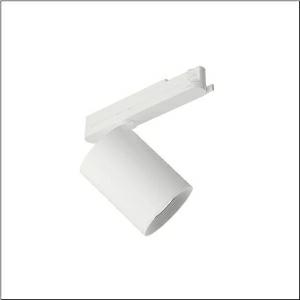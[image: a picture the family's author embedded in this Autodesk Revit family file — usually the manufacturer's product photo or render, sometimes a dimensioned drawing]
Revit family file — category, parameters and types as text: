
# Revit family: spot_21_51se13dbb5b
name_source: partatom
category: Lighting Fixtures
units: mm (PartAtom-declared; Revit-internal decimal feet)

## family parameters
Cut with Voids When Loaded = No
Host = Face
Light Source = No
Part Type = Normal
Room Calculation Point = No
Round Connector Dimension = Use Diameter
Shared = No

## types (1)
- --- (1 x LED, 5160 lm, 42.4 W, 3000K)
    Apparent Load = 42 VA
    CIE Flux Codes = 95 98 99 100 100
    Color Rendering = 90
    Color Temperature = 3000K
    Default Elevation = 1800 mm
    Description = Spot 21, directional spotlight, light control with lens, of PMMA, LED rated luminous flux: 5.120lm, light colour: 930, control gear: ECG Multilumen, with 3-phase adapter, mains connection: 220..240V, AC, 50/60Hz, of aluminium, traffic white (RAL 9016), length: 253mm, diameter: 105mm, protection rating (complete): IP20, insulation class (complete): insulation class I (protective earthing), certification: CE, impact resistance: IK02, permissible ambient temperature for indoor applications: -20..+40°C, packaging unit: 1 piece
    Height = 175 mm
    Lamp = 1 x LED
    Lamp Light Flux = 5160 lm
    Lamp Power = 42.4 W
    Lamp count = 1
    Length = 105 mm
    Luminous efficacy = 122 lm/W
    Manufacturer = Siteco
    ModVariant = No
    Model = 51SE13DBB5B
    Mounting Place = Ceiling
    Mounting Type = Pendant
    Number of Poles = 1
    OnlyDefault = Yes
    Power Factor = 1
    Product Name = Spot 21
    Product group = directional spotlight
    ProductGroupID = 905
    Protection Class = Protection class I
    Protection Degree = IP 20
    RLX_Detail_Level = 1
    RLX_Emergency_Light_Flux = 0 lm
    RLX_Emergency_Type = 0
    RLX_Emergency_Type_DB = No
    RlxData = <blob elided: 17685 chars, md5=ed2479b2>
    Socket = socket
    Standby Power = 0 W
    System Light Flux = 5160 lm
    System Power = 42 W
    Type Comments = factory setting: luminous flux: 100 % | (ON | ON | ON | ON) | 1050 mA
    Type Image = l_1003976.jpg
    URL = http://relux.com
    VarID = @adj_165601
    Voltage = 0 V
    Weight = 0.00 kg
    Width = 0 mm  [stored 0 ft]

note: [stored X ft] marks values corroborated as IEEE doubles in the binary element streams (Revit-internal decimal feet)

## geometry (parser evidence)
native form markers: Blend x4, Sweep x9
no freeform markers — native parametric forms only
